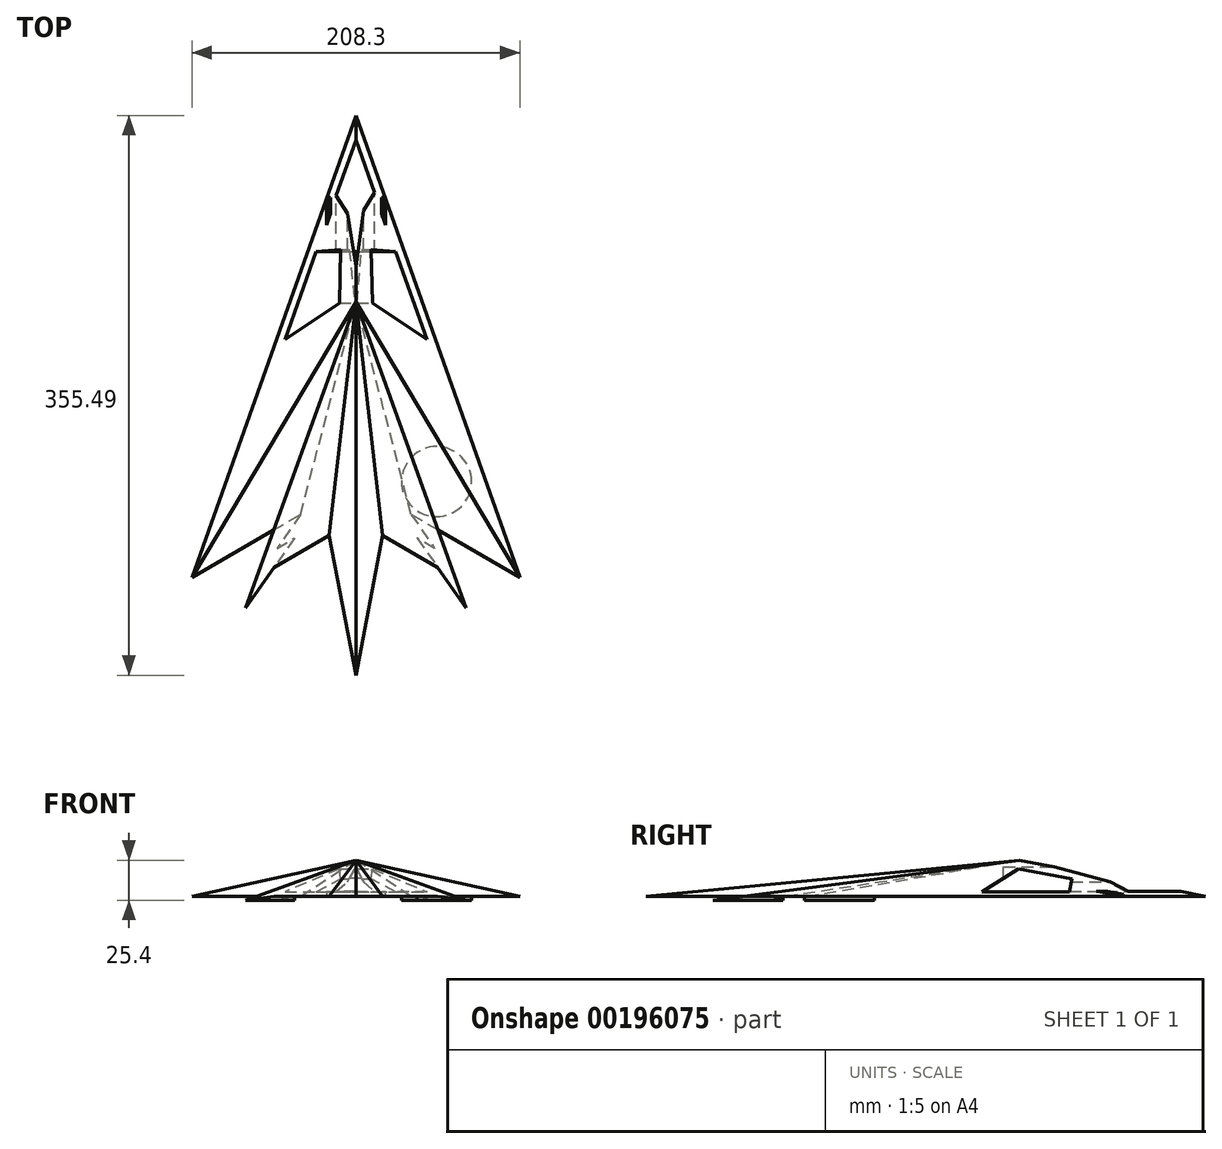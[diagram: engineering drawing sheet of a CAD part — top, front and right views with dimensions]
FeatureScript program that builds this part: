
annotation { "Feature Type Name" : "Feature", "Feature Type Description" : "" }
export const myFeature = defineFeature(function(context is Context, id is Id, definition is map)
    precondition{}
    {
        {
            var Q0;
            Q0=qCreatedBy(makeId("Top.planeOp"),FACE);
            var sketch = newSketch(context, id + "F0", { "sketchPlane" : qUnion([Q0])});
            skLineSegment(sketch, "E0", {"start": v(0, 192.23) * mm, "end": v(-115.73, -133.77) * mm});
            skLineSegment(sketch, "E1", {"start": v(-115.73, -133.77) * mm, "end": v(-38.95, -89.27) * mm});
            skLineSegment(sketch, "E2", {"start": v(-38.95, -89.27) * mm, "end": v(-70.1, -133.77) * mm});
            skLineSegment(sketch, "E3", {"start": v(-70.1, -133.77) * mm, "end": v(-18.9, -104.08) * mm});
            skLineSegment(sketch, "E4", {"start": v(-18.9, -104.08) * mm, "end": v(0, -202.76) * mm});
            skLineSegment(sketch, "E5.MirrorCS", {"start": v(0, 192.23) * mm, "end": v(115.73, -133.77) * mm});
            skLineSegment(sketch, "E6.MirrorCS", {"start": v(115.73, -133.77) * mm, "end": v(38.95, -89.27) * mm});
            skLineSegment(sketch, "E7.MirrorCS", {"start": v(38.95, -89.27) * mm, "end": v(70.1, -133.77) * mm});
            skLineSegment(sketch, "E8.MirrorCS", {"start": v(70.1, -133.77) * mm, "end": v(18.9, -104.08) * mm});
            skLineSegment(sketch, "E9.MirrorCS", {"start": v(18.9, -104.08) * mm, "end": v(0, -202.76) * mm});
            skSolve(sketch);
        }
        {
            var Q0;
            Q0=makeQuery(id+"F0.imprint","IMPRINT",FACE,{"disambiguationData":[TD([[makeQuery(id+"F0.imprint","IMPRINT",EDGE,{"derivedFrom":sQuery(id+"F0.wireOp",EDGE,"E0")}),1.0]])]});
            cPlane(context, id + "F1", {"entities" : qUnion([Q0]), "cplaneType" : CPlaneType.OFFSET, "offset" : 25.4 * mm, "width" : 152.4 * mm, "height" : 152.4 * mm});
        }
        {
            var Q0;
            Q0=qCreatedBy(id+"F1.planeOp",FACE);
            var sketch = newSketch(context, id + "F2", { "sketchPlane" : qUnion([Q0])});
            skPoint(sketch, "E10", {"position": v(0, 60.76) * mm});
            skSolve(sketch);
        }
        {
            var Q0;
            Q0=makeQuery(id+"F0.imprint","IMPRINT",FACE,{"disambiguationData":[TD([[makeQuery(id+"F0.imprint","IMPRINT",EDGE,{"derivedFrom":sQuery(id+"F0.wireOp",EDGE,"E0")}),1.0]])]});
            var Q1;
            Q1=sQuery(id+"F2.wireOp",VERTEX,"E10");
            loft(context, id + "F3", {"sheetProfilesArray" : [{ "sheetProfileEntities" : qUnion([Q0]) }, { "sheetProfileEntities" : qUnion([Q1]) }]});
        }
        {
            var Q0;
            Q0=qCreatedBy(makeId("Right.planeOp"),FACE);
            cPlane(context, id + "F4", {"entities" : qUnion([Q0]), "cplaneType" : CPlaneType.OFFSET, "offset" : 50.8 * mm, "width" : 152.4 * mm, "height" : 152.4 * mm});
        }
        {
            var Q0;
            Q0=qCreatedBy(id+"F4.planeOp",FACE);
            var sketch = newSketch(context, id + "F5", { "sketchPlane" : qUnion([Q0])});
            skLineSegment(sketch, "E11", {"start": v(60.17, 19.84) * mm, "end": v(94.17, 13.65) * mm});
            skLineSegment(sketch, "E12", {"start": v(94.17, 13.65) * mm, "end": v(92.68, 5.45) * mm});
            skLineSegment(sketch, "E13", {"start": v(92.68, 5.45) * mm, "end": v(36.99, 5.45) * mm});
            skLineSegment(sketch, "E14", {"start": v(36.99, 5.45) * mm, "end": v(60.17, 19.84) * mm});
            skSolve(sketch);
        }
        {
            var Q0;
            Q0=makeQuery(id+"F5.imprint","IMPRINT",FACE,{"disambiguationData":[TD([[makeQuery(id+"F5.imprint","IMPRINT",EDGE,{"derivedFrom":sQuery(id+"F5.wireOp",EDGE,"E11")}),-1.0]])]});
            extrude(context, id + "F6", {"entities" : qUnion([Q0]), "operationType" : NewBodyOperationType.REMOVE, "endBound" : BoundingType.THROUGH_ALL, "oppositeDirection" : true, "depth" : 25.4 * mm});
        }
        {
            var Q0;
            Q0=qCreatedBy(makeId("Front.planeOp"),FACE);
            cPlane(context, id + "F7", {"entities" : qUnion([Q0]), "cplaneType" : CPlaneType.OFFSET, "offset" : 152.4 * mm, "oppositeDirection" : true, "width" : 152.4 * mm, "height" : 152.4 * mm});
        }
        {
            var Q0;
            Q0=qCreatedBy(id+"F7.planeOp",FACE);
            var sketch = newSketch(context, id + "F8", { "sketchPlane" : qUnion([Q0])});
            skLineSegment(sketch, "E15", {"start": v(11.81, 5.57) * mm, "end": v(-12.49, 5.57) * mm});
            skPoint(sketch, "E16.startSnap0", {"position": v(-0.34, 5.57) * mm});
            skPoint(sketch, "E16.endSnap0", {"position": v(-0.34, 5.57) * mm});
            skLineSegment(sketch, "E17", {"start": v(11.81, 5.57) * mm, "end": v(4.72, 11.64) * mm});
            skLineSegment(sketch, "E18", {"start": v(-12.49, 5.57) * mm, "end": v(-5.4, 11.64) * mm});
            skLineSegment(sketch, "E19", {"start": v(4.72, 11.64) * mm, "end": v(0, 21.1) * mm});
            skLineSegment(sketch, "E20", {"start": v(0, 21.1) * mm, "end": v(-5.4, 11.64) * mm});
            skSolve(sketch);
        }
        {
            var Q0;
            Q0=makeQuery(id+"F8.imprint","IMPRINT",FACE,{"disambiguationData":[TD([[makeQuery(id+"F8.imprint","IMPRINT",EDGE,{"derivedFrom":sQuery(id+"F8.wireOp",EDGE,"E15")}),-1.0]])]});
            extrude(context, id + "F9", {"entities" : qUnion([Q0]), "operationType" : NewBodyOperationType.REMOVE, "depth" : 101.6 * mm});
        }
        {
            var Q0;
            Q0=makeQuery(id+"F9.boolean.opBoolean","COPY",FACE,{"derivedFrom":makeQuery(id+"F9.opExtrude","CAP_FACE",FACE,{"disambiguationData":[OSD([sQuery(id+"F8.wireOp",EDGE,"E15"),sQuery(id+"F8.wireOp",EDGE,"E17"),sQuery(id+"F8.wireOp",EDGE,"E18"),sQuery(id+"F8.wireOp",EDGE,"E19"),sQuery(id+"F8.wireOp",EDGE,"E20")])],"isStart":true})});
            extrude(context, id + "F10", {"entities" : qUnion([Q0]), "operationType" : NewBodyOperationType.REMOVE, "endBound" : BoundingType.THROUGH_ALL, "oppositeDirection" : true, "depth" : 25.4 * mm});
        }
        {
            var Q0;
            Q0=qCreatedBy(id+"F7.planeOp",FACE);
            cPlane(context, id + "F11", {"entities" : qUnion([Q0]), "cplaneType" : CPlaneType.OFFSET, "offset" : 25.4 * mm, "width" : 152.4 * mm, "height" : 152.4 * mm});
        }
        {
            var Q0;
            Q0=qCreatedBy(id+"F11.planeOp",FACE);
            var sketch = newSketch(context, id + "F12", { "sketchPlane" : qUnion([Q0])});
            skLineSegment(sketch, "E21.bottom", {"start": v(18.74, 5.75) * mm, "end": v(16.2, 5.75) * mm});
            skLineSegment(sketch, "E21.top", {"start": v(18.74, 3.2) * mm, "end": v(16.2, 3.2) * mm});
            skLineSegment(sketch, "E21.left", {"start": v(18.74, 5.75) * mm, "end": v(18.74, 3.2) * mm});
            skLineSegment(sketch, "E21.right", {"start": v(16.2, 5.75) * mm, "end": v(16.2, 3.2) * mm});
            skLineSegment(sketch, "E22.MirrorCS", {"start": v(-16.2, 5.75) * mm, "end": v(-16.2, 3.2) * mm});
            skLineSegment(sketch, "E23.MirrorCS", {"start": v(-18.74, 5.75) * mm, "end": v(-18.74, 3.2) * mm});
            skLineSegment(sketch, "E24.MirrorCS", {"start": v(-18.74, 5.75) * mm, "end": v(-16.2, 5.75) * mm});
            skLineSegment(sketch, "E25.MirrorCS", {"start": v(-18.74, 3.2) * mm, "end": v(-16.2, 3.2) * mm});
            skSolve(sketch);
        }
        {
            var Q0;
            Q0=makeQuery(id+"F12.imprint","IMPRINT",FACE,{"disambiguationData":[TD([[makeQuery(id+"F12.imprint","IMPRINT",EDGE,{"derivedFrom":sQuery(id+"F12.wireOp",EDGE,"E21.bottom")}),1.0]])]});
            var Q1;
            Q1=makeQuery(id+"F12.imprint","IMPRINT",FACE,{"disambiguationData":[TD([[makeQuery(id+"F12.imprint","IMPRINT",EDGE,{"derivedFrom":sQuery(id+"F12.wireOp",EDGE,"E22.MirrorCS")}),-1.0]])]});
            extrude(context, id + "F13", {"entities" : qUnion([Q0, Q1]), "operationType" : NewBodyOperationType.ADD, "depth" : 25.4 * mm});
        }
        {
            var Q0;
            Q0=makeQuery(id+"F13.opExtrude","CAP_FACE",FACE,{"disambiguationData":[OSD([sQuery(id+"F12.wireOp",EDGE,"E21.bottom"),sQuery(id+"F12.wireOp",EDGE,"E21.top"),sQuery(id+"F12.wireOp",EDGE,"E21.left"),sQuery(id+"F12.wireOp",EDGE,"E21.right")])],"isStart":true});
            var Q1;
            Q1=makeQuery(id+"F13.opExtrude","CAP_FACE",FACE,{"disambiguationData":[OSD([sQuery(id+"F12.wireOp",EDGE,"E22.MirrorCS"),sQuery(id+"F12.wireOp",EDGE,"E23.MirrorCS"),sQuery(id+"F12.wireOp",EDGE,"E24.MirrorCS"),sQuery(id+"F12.wireOp",EDGE,"E25.MirrorCS")])],"isStart":true});
            extrude(context, id + "F14", {"entities" : qUnion([Q0, Q1]), "operationType" : NewBodyOperationType.REMOVE, "oppositeDirection" : true, "depth" : 12.7 * mm});
        }
        {
            var Q0;
            Q0=makeQuery(id+"F3.opLoft","CAP_FACE",FACE,{"disambiguationData":[OSD([makeQuery(id+"F0.imprint","IMPRINT",FACE,{"disambiguationData":[TD([[makeQuery(id+"F0.imprint","IMPRINT",EDGE,{"derivedFrom":sQuery(id+"F0.wireOp",EDGE,"E0")}),1.0]])]})])],"isStart":true});
            var sketch = newSketch(context, id + "F15", { "sketchPlane" : qUnion([Q0])});
            skCircle(sketch, "E26", {"center": v(-51.25, 53.33) * mm, "radius": 22.23 * mm});
            skCircle(sketch, "E27.MirrorC", {"center": v(51.25, 53.33) * mm, "radius": 22.23 * mm});
            skCircle(sketch, "E28", {"center": v(0, 0.05) * mm, "radius": 22.23 * mm});
            skCircle(sketch, "E29", {"center": v(0, -88.44) * mm, "radius": 22.23 * mm});
            skSolve(sketch);
        }
        {
            var Q0;
            Q0=makeQuery(id+"F15.imprint","IMPRINT",FACE,{"disambiguationData":[TD([[makeQuery(id+"F15.imprint","IMPRINT",EDGE,{"derivedFrom":sQuery(id+"F15.wireOp",EDGE,"E26")}),1.0]])]});
            var Q1;
            Q1=makeQuery(id+"F15.imprint","IMPRINT",FACE,{"disambiguationData":[TD([[makeQuery(id+"F15.imprint","IMPRINT",EDGE,{"derivedFrom":sQuery(id+"F15.wireOp",EDGE,"E27.MirrorC")}),-1.0]])]});
            var Q2;
            Q2=makeQuery(id+"F15.imprint","IMPRINT",FACE,{"disambiguationData":[TD([[makeQuery(id+"F15.imprint","IMPRINT",EDGE,{"derivedFrom":sQuery(id+"F15.wireOp",EDGE,"E28")}),1.0]])]});
            var Q3;
            Q3=makeQuery(id+"F15.imprint","IMPRINT",FACE,{"disambiguationData":[TD([[makeQuery(id+"F15.imprint","IMPRINT",EDGE,{"derivedFrom":sQuery(id+"F15.wireOp",EDGE,"E29")}),1.0]])]});
            extrude(context, id + "F16", {"entities" : qUnion([Q0, Q1, Q2, Q3]), "operationType" : NewBodyOperationType.REMOVE, "oppositeDirection" : true, "depth" : 2.54 * mm});
        }
        {
            var Q0;
            Q0=qCreatedBy(makeId("Front.planeOp"),FACE);
            cPlane(context, id + "F17", {"entities" : qUnion([Q0]), "cplaneType" : CPlaneType.OFFSET, "offset" : 76.2 * mm, "width" : 152.4 * mm, "height" : 152.4 * mm});
        }
        {
            var Q0;
            Q0=qCreatedBy(id+"F17.planeOp",FACE);
            var sketch = newSketch(context, id + "F18", { "sketchPlane" : qUnion([Q0])});
            skCircle(sketch, "E30", {"center": v(0, 10.63) * mm, "radius": 9.53 * mm});
            skSolve(sketch);
        }
        {
            var Q0;
            Q0=sQuery(id+"F18.wireOp",EDGE,"E30");
            extrude(context, id + "F19", {"bodyType" : ToolBodyType.SURFACE, "surfaceEntities" : qUnion([Q0]), "endBound" : BoundingType.SYMMETRIC, "depth" : 101.6 * mm});
        }
    });
